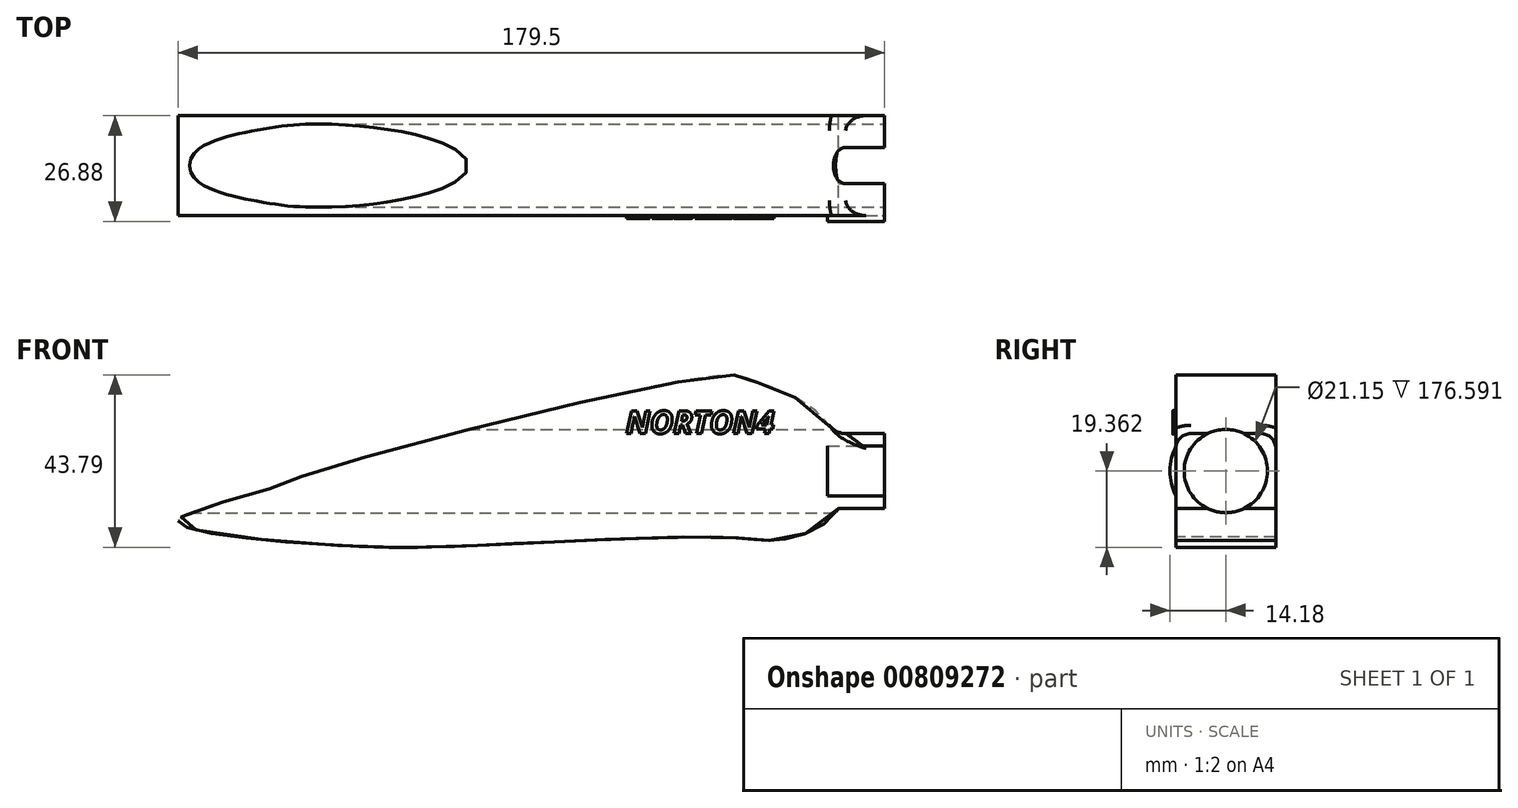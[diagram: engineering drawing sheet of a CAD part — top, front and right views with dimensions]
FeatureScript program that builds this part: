
annotation { "Feature Type Name" : "Feature", "Feature Type Description" : "" }
export const myFeature = defineFeature(function(context is Context, id is Id, definition is map)
    precondition{}
    {
        {
            var Q0;
            Q0=qCreatedBy(makeId("Front.planeOp"),FACE);
            var sketch = newSketch(context, id + "F0", { "sketchPlane" : qUnion([Q0])});
            skFitSpline(sketch, "E0", {"points": [v(-78.93, 20.97) * mm, v(-40.83, 14.9) * mm, v(0, 14.9) * mm, v(61.38, 16.72) * mm, v(73.32, 16.13) * mm, v(88.81, 24.1) * mm, v(85.34, 46.75) * mm, v(67.56, 56.47) * mm, v(59.12, 57.97) * mm, v(-42.48, 33.94) * mm, v(-59.22, 28.04) * mm, v(-78.93, 20.97) * mm]});
            skLineSegment(sketch, "E1.bottom", {"start": v(87.86, 43.16) * mm, "end": v(100.56, 43.16) * mm});
            skLineSegment(sketch, "E1.top", {"start": v(87.86, 24.1) * mm, "end": v(100.56, 24.1) * mm});
            skLineSegment(sketch, "E1.left", {"start": v(87.86, 43.16) * mm, "end": v(87.86, 24.1) * mm});
            skLineSegment(sketch, "E1.right", {"start": v(100.56, 43.16) * mm, "end": v(100.56, 24.1) * mm});
            skLineSegment(sketch, "E2", {"start": v(100.56, 33.63) * mm, "end": v(-125.45, 25.6) * mm, "construction": true});
            skLineSegment(sketch, "E3", {"start": v(-21.54, 29.48) * mm, "end": v(-21.54, 29.29) * mm, "construction": true});
            skLineSegment(sketch, "E4", {"start": v(87.86, 43.16) * mm, "end": v(-86.4, 36.96) * mm, "construction": true});
            skLineSegment(sketch, "E5", {"start": v(87.86, 24.1) * mm, "end": v(-97.15, 24.1) * mm, "construction": true});
            skSolve(sketch);
        }
        {
            var Q0;
            {var subQ0=sQuery(id+"F0.wireOp",EDGE,"E1.left");var subQ1=sQuery(id+"F0.wireOp",EDGE,"E0");var subQ3=makeQuery(id+"F0.imprint","INTERSECT",VERTEX,{"derivedFrom":[subQ1,subQ0]});Q0=makeQuery(id+"F0.imprint","IMPRINT",FACE,{"disambiguationData":[TD([[makeQuery(id+"F0.imprint","IMPRINT",EDGE,{"disambiguationData":[TD([[subQ3,-1.0]])],"derivedFrom":subQ1}),1.0]])]});}
            var Q1;
            {var subQ0=sQuery(id+"F0.wireOp",EDGE,"E1.left");var subQ1=sQuery(id+"F0.wireOp",EDGE,"E0");var subQ3=makeQuery(id+"F0.imprint","INTERSECT",VERTEX,{"derivedFrom":[subQ1,subQ0]});Q1=makeQuery(id+"F0.imprint","IMPRINT",FACE,{"disambiguationData":[TD([[makeQuery(id+"F0.imprint","IMPRINT",EDGE,{"disambiguationData":[TD([[subQ3,1.0]])],"derivedFrom":subQ1}),1.0]])]});}
            var Q2;
            {var subQ1=sQuery(id+"F0.wireOp",EDGE,"E1.bottom");Q2=makeQuery(id+"F0.imprint","IMPRINT",FACE,{"disambiguationData":[TD([[makeQuery(id+"F0.imprint","IMPRINT",EDGE,{"derivedFrom":subQ1}),-1.0]])]});}
            extrude(context, id + "F1", {"entities" : qUnion([Q0, Q1, Q2]), "depth" : 25.4 * mm, "offsetDistance" : 25.4 * mm});
        }
        {
            var Q0;
            Q0=makeQuery(id+"F1.opExtrude","SWEPT_FACE",FACE,{"disambiguationData":[OSD([sQuery(id+"F0.wireOp",EDGE,"E1.right")])]});
            var sketch = newSketch(context, id + "F2", { "sketchPlane" : qUnion([Q0])});
            skCircle(sketch, "E6", {"center": v(-12.7, 33.63) * mm, "radius": 7.54 * mm});
            skPoint(sketch, "E6.centerSnap0", {"position": v(-12.7, 43.16) * mm});
            skPoint(sketch, "E6.centerSnap1", {"position": v(-25.4, 33.63) * mm});
            skSolve(sketch);
        }
        {
            var Q0;
            Q0 = qSketchRegion(id + "F2", true);
            extrude(context, id + "F3", {"entities" : qUnion([Q0]), "operationType" : NewBodyOperationType.REMOVE, "oppositeDirection" : true, "depth" : 178.82 * mm, "offsetDistance" : 25.4 * mm});
        }
        {
            var Q0;
            Q0=makeQuery(id+"F1.opExtrude","CAP_FACE",FACE,{"disambiguationData":[OSD([sQuery(id+"F0.wireOp",EDGE,"E0"),sQuery(id+"F0.wireOp",EDGE,"E1.bottom"),sQuery(id+"F0.wireOp",EDGE,"E1.top"),sQuery(id+"F0.wireOp",EDGE,"E1.left"),sQuery(id+"F0.wireOp",EDGE,"E1.right")])],"isStart":false});
            var sketch = newSketch(context, id + "F4", { "sketchPlane" : qUnion([Q0])});
            skText(sketch, "E7", { "text": "NORTON4", "fontName": "OpenSans-BoldItalic.ttf"});
            const initialGuessF4  = {"E7": [0.0348, 0.04314, 1, 0, 0.00583]};
            skSetInitialGuess(sketch, initialGuessF4);
            skSolve(sketch);
        }
        {
            var Q0;
            Q0=makeQuery(id+"F1.opExtrude","CAP_EDGE",EDGE,{"disambiguationData":[OSD([sQuery(id+"F0.wireOp",EDGE,"E1.bottom")])],"isStart":false});
            var Q1;
            Q1=makeQuery(id+"F1.opExtrude","CAP_EDGE",EDGE,{"disambiguationData":[OSD([sQuery(id+"F0.wireOp",EDGE,"E1.bottom")])],"isStart":true});
            fillet(context, id + "F5", {"entities" : qUnion([Q0, Q1]), "radius" : 3.8 * mm, "tangentPropagation" : true, "allowEdgeOverflow" : false});
        }
        {
            var Q0;
            Q0=makeQuery(id+"F1.opExtrude","SWEPT_EDGE",EDGE,{"disambiguationData":[OSD([sQuery(id+"F0.wireOp",EDGE,"E0"),sQuery(id+"F0.wireOp",EDGE,"E1.bottom"),sQuery(id+"F0.wireOp",EDGE,"E1.left")])]});
            fillet(context, id + "F6", {"entities" : qUnion([Q0]), "radius" : 5.08 * mm, "tangentPropagation" : true, "allowEdgeOverflow" : false});
        }
        {
            var Q0;
            Q0 = qSketchRegion(id + "F4", true);
            extrude(context, id + "F7", {"entities" : qUnion([Q0]), "operationType" : NewBodyOperationType.ADD, "depth" : 0.76 * mm, "offsetDistance" : 25.4 * mm});
        }
        {
            var Q0;
            Q0=makeQuery(id+"F1.opExtrude","SWEPT_FACE",FACE,{"disambiguationData":[OSD([sQuery(id+"F0.wireOp",EDGE,"E1.right")])]});
            var sketch = newSketch(context, id + "F8", { "sketchPlane" : qUnion([Q0])});
            skCircle(sketch, "E8", {"center": v(-12.7, 33.63) * mm, "radius": 10.58 * mm});
            skSolve(sketch);
        }
        {
            var Q0;
            Q0 = qSketchRegion(id + "F8", true);
            extrude(context, id + "F9", {"entities" : qUnion([Q0]), "operationType" : NewBodyOperationType.REMOVE, "oppositeDirection" : true, "depth" : 192.53 * mm, "offsetDistance" : 25.4 * mm});
        }
        {
            var Q0;
            {var subQ1=sQuery(id+"F0.wireOp",EDGE,"E1.bottom");var subQ2=sQuery(id+"F0.wireOp",EDGE,"E1.right");Q0=makeQuery(id+"F9.boolean.opBoolean","SPLIT",FACE,{"disambiguationData":[TD([makeQuery(id+"F5.opFillet","BLEND_FACE",FACE,{"disambiguationData":[OSD([subQ1]),TDD([makeQuery(id+"F1.opExtrude","CAP_EDGE",EDGE,{"disambiguationData":[OSD([subQ1])],"isStart":false})])]})])],"derivedFrom":makeQuery(id+"F1.opExtrude","SWEPT_FACE",FACE,{"disambiguationData":[OSD([subQ2])]})});}
            var sketch = newSketch(context, id + "F10", { "sketchPlane" : qUnion([Q0])});
            skCircle(sketch, "E9", {"center": v(-12.7, 33.63) * mm, "radius": 14.18 * mm});
            skSolve(sketch);
        }
        {
            var Q0;
            {var subQ0=sQuery(id+"F10.wireOp",EDGE,"E9");var subQ1=sQuery(id+"F0.wireOp",EDGE,"E1.right");var subQ4=makeQuery(id+"F1.opExtrude","CAP_EDGE",EDGE,{"disambiguationData":[OSD([subQ1])],"isStart":false});var subQ5=makeQuery(id+"F10.imprint","INTERSECT",VERTEX,{"derivedFrom":[subQ4,subQ0]});Q0=makeQuery(id+"F10.imprint","IMPRINT",FACE,{"disambiguationData":[TD([[makeQuery(id+"F10.imprint","IMPRINT",EDGE,{"disambiguationData":[TD([[subQ5,1.0]])],"derivedFrom":subQ0}),1.0]])]});}
            var Q1;
            {var subQ2=sQuery(id+"F8.wireOp",EDGE,"E8");var subQ13=makeQuery(id+"F9.boolean.opBoolean","COPY",EDGE,{"disambiguationData":[OD(1.0)],"derivedFrom":makeQuery(id+"F9.opExtrude","CAP_EDGE",EDGE,{"disambiguationData":[OSD([subQ2])],"isStart":true})});Q1=makeQuery(id+"F10.imprint","IMPRINT",FACE,{"disambiguationData":[TD([[makeQuery(id+"F10.imprint","IMPRINT",EDGE,{"derivedFrom":subQ13}),-1.0]])]});}
            var Q2;
            {var subQ2=sQuery(id+"F8.wireOp",EDGE,"E8");var subQ10=makeQuery(id+"F9.boolean.opBoolean","COPY",EDGE,{"disambiguationData":[OD(1.0)],"derivedFrom":makeQuery(id+"F9.opExtrude","CAP_EDGE",EDGE,{"disambiguationData":[OSD([subQ2])],"isStart":true})});Q2=makeQuery(id+"F10.imprint","IMPRINT",FACE,{"disambiguationData":[TD([[makeQuery(id+"F10.imprint","IMPRINT",EDGE,{"derivedFrom":subQ10}),1.0]])]});}
            extrude(context, id + "F11", {"entities" : qUnion([Q0, Q1, Q2]), "oppositeDirection" : true, "depth" : 14.48 * mm, "offsetDistance" : 25.4 * mm});
        }
        {
            var Q0;
            Q0=makeQuery(id+"F11.opExtrude","CAP_FACE",FACE,{"disambiguationData":[OSD([sQuery(id+"F10.wireOp",EDGE,"E9")])],"isStart":true});
            var sketch = newSketch(context, id + "F12", { "sketchPlane" : qUnion([Q0])});
            skCircle(sketch, "E10", {"center": v(-12.7, 33.63) * mm, "radius": 10.37 * mm});
            skSolve(sketch);
        }
        {
            var Q0;
            Q0 = qSketchRegion(id + "F12", true);
            extrude(context, id + "F13", {"entities" : qUnion([Q0]), "operationType" : NewBodyOperationType.REMOVE, "oppositeDirection" : true, "depth" : 25.4 * mm, "offsetDistance" : 25.4 * mm});
        }
    });
